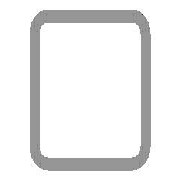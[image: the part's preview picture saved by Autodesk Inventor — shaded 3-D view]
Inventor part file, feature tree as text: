
AUTODESK INVENTOR PART (.ipt)
format: ipt  version: 2022.1 (Build 261234000, 234)  size: 134,656 bytes
history: native  units: mm (DEFAULTED — no unit token found)
features: other x4, sketch x3, extrude x1, plane x1
ambient origin geometry x8: Origin, YZ Plane, XZ Plane, XY Plane, X Axis, Y Axis, Z Axis, Center Point
bodies: Solid1 (feature_tree)
feature tree (9):
  parser-record x1  (decoder bookkeeping rows leaked as tree rows — omitted from the tree; the rows remain in map.json)
  other  "Driven Length"
  other  "Plano inicial"
  other  "Plano final"
  extrude  "Cuerpo"  TaperAngle=0.0deg  [1 undecoded]
  sketch  "Boceto"  dims[d10=40.0mm d11=40.0mm d12=5.0mm d13=-0.0mm d14=480.0mm d15=20.0mm d16=20.0mm d17=90.0deg d18=480.0mm]
  sketch  "Sketch3"  dims[d3=480.0mm d4=0.0mm]
  plane  "Work Plane3"
  sketch  "Sketch4"  dims[d7=7.5mm]
note: 1 required parameter value undecoded (feature->parameter linkage not recoverable at this tier; creation-order binding heuristic only, values carry confidence <= 0.55)
